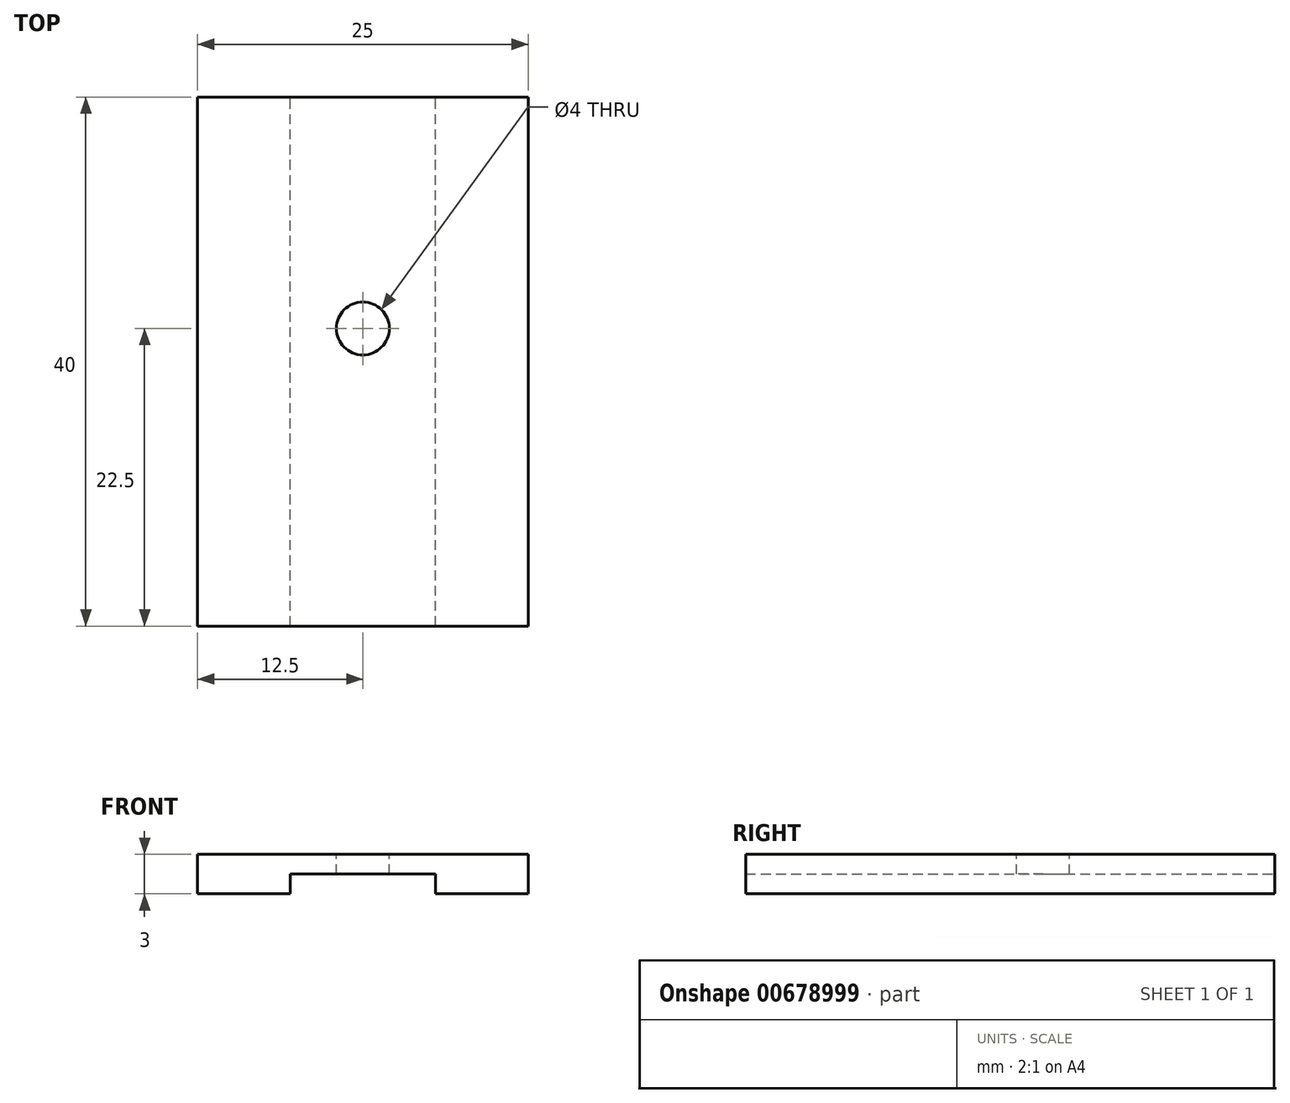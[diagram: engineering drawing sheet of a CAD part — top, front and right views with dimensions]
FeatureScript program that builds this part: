
annotation { "Feature Type Name" : "Feature", "Feature Type Description" : "" }
export const myFeature = defineFeature(function(context is Context, id is Id, definition is map)
    precondition{}
    {
        {
            var Q0;
            Q0=qCreatedBy(makeId("Top.planeOp"),FACE);
            var sketch = newSketch(context, id + "F0", { "sketchPlane" : qUnion([Q0])});
            skPoint(sketch, "E0.middle", {"position": v(0, 0) * mm});
            skLineSegment(sketch, "E1.bottom", {"start": v(12.5, -20) * mm, "end": v(-12.5, -20) * mm});
            skLineSegment(sketch, "E1.top", {"start": v(12.5, 20) * mm, "end": v(-12.5, 20) * mm});
            skLineSegment(sketch, "E1.left", {"start": v(12.5, -20) * mm, "end": v(12.5, 20) * mm});
            skLineSegment(sketch, "E1.right", {"start": v(-12.5, -20) * mm, "end": v(-12.5, 20) * mm});
            skSolve(sketch);
        }
        {
            var Q0;
            Q0 = qSketchRegion(id + "F0", true);
            extrude(context, id + "F1", {"entities" : qUnion([Q0]), "depth" : 3 * mm, "offsetDistance" : 25 * mm});
        }
        {
            var Q0;
            Q0=makeQuery(id+"F1.opExtrude","CAP_FACE",FACE,{"disambiguationData":[OSD([sQuery(id+"F0.wireOp",EDGE,"E1.bottom"),sQuery(id+"F0.wireOp",EDGE,"E1.top"),sQuery(id+"F0.wireOp",EDGE,"E1.left"),sQuery(id+"F0.wireOp",EDGE,"E1.right")])],"isStart":true});
            var sketch = newSketch(context, id + "F2", { "sketchPlane" : qUnion([Q0])});
            skLineSegment(sketch, "E2.bottom", {"start": v(5.5, 20) * mm, "end": v(-5.5, 20) * mm});
            skLineSegment(sketch, "E2.top", {"start": v(5.5, -20) * mm, "end": v(-5.5, -20) * mm});
            skLineSegment(sketch, "E2.left", {"start": v(5.5, 20) * mm, "end": v(5.5, -20) * mm});
            skLineSegment(sketch, "E2.right", {"start": v(-5.5, 20) * mm, "end": v(-5.5, -20) * mm});
            skPoint(sketch, "E2.middle", {"position": v(0, 0) * mm});
            skSolve(sketch);
        }
        {
            var Q0;
            Q0 = qSketchRegion(id + "F2", true);
            extrude(context, id + "F3", {"entities" : qUnion([Q0]), "operationType" : NewBodyOperationType.REMOVE, "oppositeDirection" : true, "depth" : 1.5 * mm, "offsetDistance" : 25 * mm});
        }
        {
            var Q0;
            Q0=makeQuery(id+"F1.opExtrude","CAP_FACE",FACE,{"disambiguationData":[OSD([sQuery(id+"F0.wireOp",EDGE,"E1.bottom"),sQuery(id+"F0.wireOp",EDGE,"E1.top"),sQuery(id+"F0.wireOp",EDGE,"E1.left"),sQuery(id+"F0.wireOp",EDGE,"E1.right")])],"isStart":false});
            var sketch = newSketch(context, id + "F4", { "sketchPlane" : qUnion([Q0])});
            skCircle(sketch, "E3", {"center": v(0, 2.5) * mm, "radius": 2 * mm});
            skSolve(sketch);
        }
        {
            var Q0;
            Q0 = qSketchRegion(id + "F4", true);
            extrude(context, id + "F5", {"entities" : qUnion([Q0]), "operationType" : NewBodyOperationType.REMOVE, "endBound" : BoundingType.THROUGH_ALL, "oppositeDirection" : true, "depth" : 25 * mm, "offsetDistance" : 25 * mm});
        }
    });
